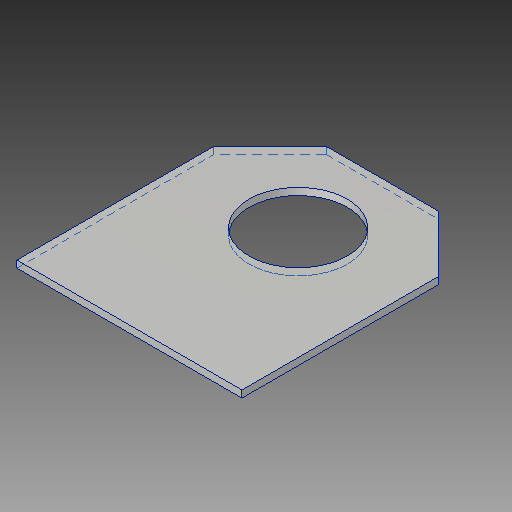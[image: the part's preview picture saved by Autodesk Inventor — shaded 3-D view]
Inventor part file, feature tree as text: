
AUTODESK INVENTOR PART (.ipt)
format: ipt  version: 2019 (Build 230136000, 136)  size: 108,544 bytes
history: native  units: in
note: dims shown in document units (in); Inventor stores cm internally (conversion verified against a paired STEP export)
features: extrude x1, chamfer x1, sketch x1
ambient origin geometry x8: Origin, YZ Plane, XZ Plane, XY Plane, X Axis, Y Axis, Z Axis, Center Point
bodies: Solid1 (feature_tree)
feature tree (3):
  extrude  "Extrusion1"  Depth=0.0625in
  chamfer  "Chamfer1"  Distance=1.0in
  sketch  "Sketch1"  dims[d0=1.0in d1=0.875in d2=1.0in d3=2.25in d4=2.0in d5=0.0625in d6=0.0in d7=0.5in d8=0.125in d9=45.0deg]
